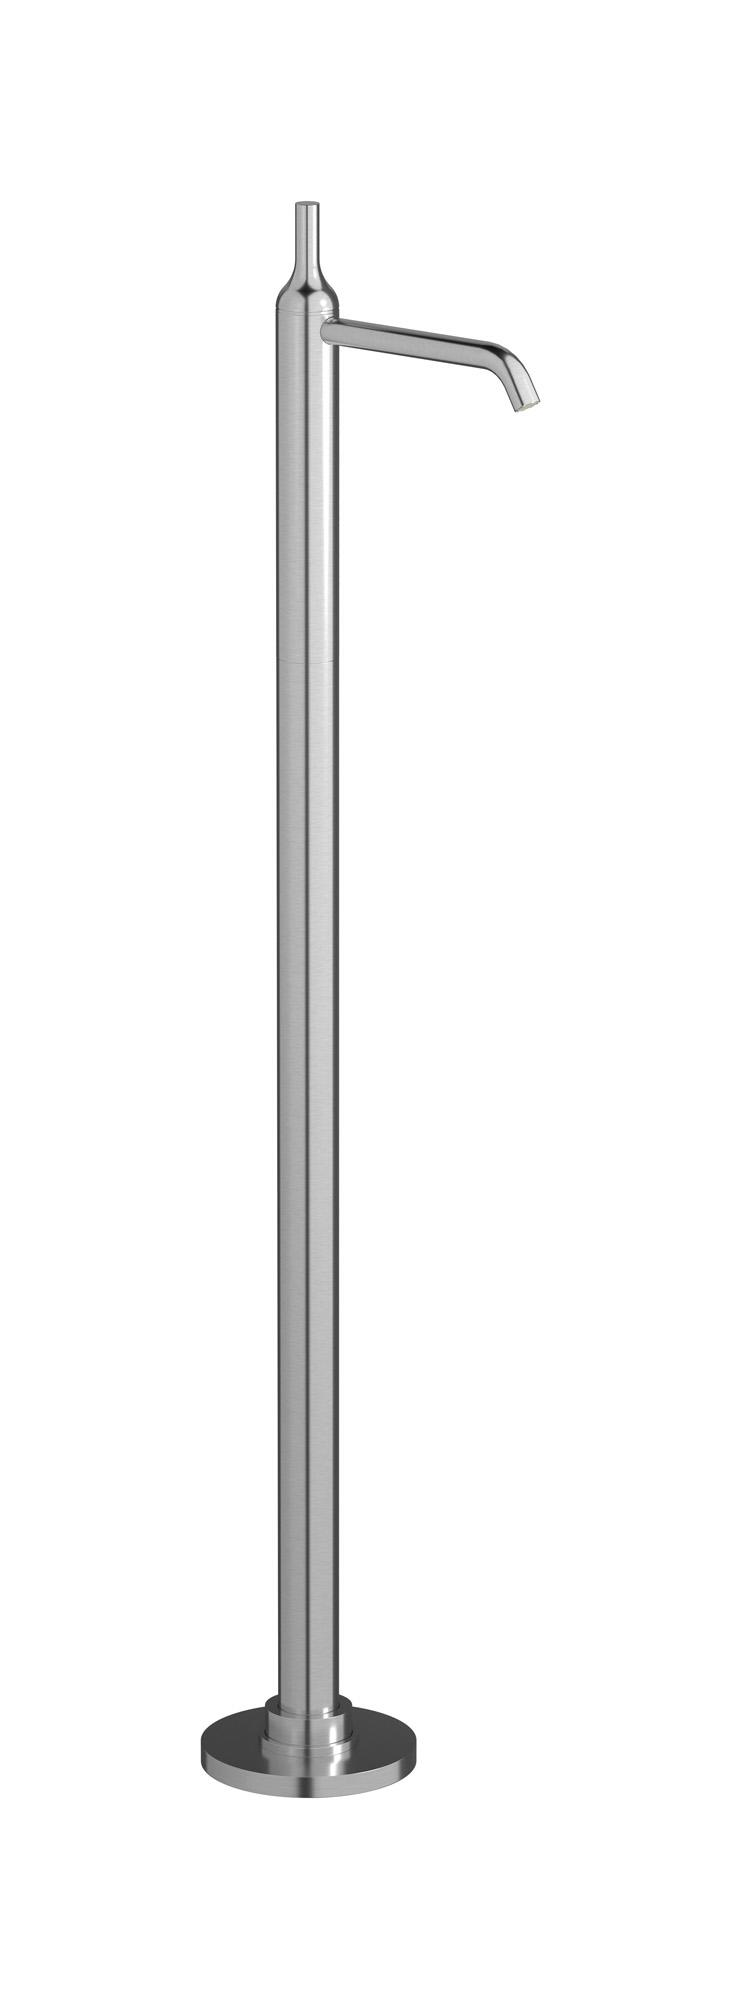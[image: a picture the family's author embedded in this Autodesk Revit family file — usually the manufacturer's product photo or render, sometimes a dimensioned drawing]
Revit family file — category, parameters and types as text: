
# Revit family: BI299
name_source: partatom
category: Apparecchi idraulici
units: mm (PartAtom-declared; Revit-internal decimal feet)

## family parameters
Basato su piano di lavoro = No
Condiviso = No
Mantieni orientamento annotazione = No
Numero OmniClass = 23.45.55.17
Punto di calcolo locali = No
Quota connettore circolare = Usa diametro
Sempre verticale = Sì
Taglio con vuoti quando caricato = No
Tipo di parte = Normale
Titolo OmniClass = Mixing Faucets

## types (4) — shared parameters
Cold water inlet = 10 mm  [stored 0.0328084 ft]
Commenti sul tipo = Washbasin mixer
Connessione CW = No
Connessione HW = No
Connessione di scarico = No
Connessione di ventilazione = No
Descrizione = Monohole freestanding washbasin mixer complete with drain
Hot water inlet = 10 mm  [stored 0.0328084 ft]
Produttore = IB Rubinetterie S.p.A.
URL = https://www.weareib.it
zero-valued in all types: Prospetto di default

## per-type parameters (varying)
| type | Finishes surface | Immagine tipo | Modello |
| Chrome | IB_Chrome | BI299CC.jpg | BI299CC |
| Brushed nickel | IB_Brushed nickel | BI299SS.jpg | BI299SS |
| Matt white | IB_matt white | BI299BO.jpg | BI299BO |
| Matt black | IB_matt black | BI299NP.jpg | BI299NP |

note: [stored X ft] marks values corroborated as IEEE doubles in the binary element streams (Revit-internal decimal feet)
